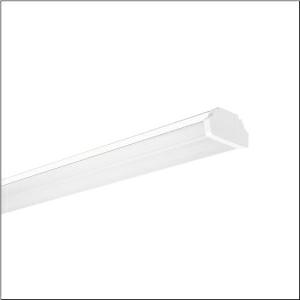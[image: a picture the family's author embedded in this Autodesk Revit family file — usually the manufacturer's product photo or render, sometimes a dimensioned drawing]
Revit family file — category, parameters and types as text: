
# Revit family: dus_31_gen_2_53bd812cv49xc2_ea29
name_source: partatom
category: Lighting Fixtures
units: mm (PartAtom-declared; Revit-internal decimal feet)

## family parameters
Cut with Voids When Loaded = No
Host = Face
Light Source = No
Part Type = Normal
Room Calculation Point = No
Round Connector Dimension = Use Diameter
Shared = No

## types (1)
- --- (1 x LED, 9240 lm, 49.9 W, 4000K)
    Apparent Load = 50 VA
    CIE Flux Codes = 47 80 95 93 100
    Color Rendering = 80
    Color Temperature = 4000K
    Default Elevation = 1800 mm
    Description = DUS 31 Gen.2, luminaire insert, of sheet steel, coil coated, white, length: 1.535mm, width: 81mm, height: 90mm, 5x system unit, system units: 307mm, LED rated luminous flux: 9.240lm, light colour: 840, SDCM (Standard Deviation of Colour Matching)MacAdam ≤ 3 SDCM (initial), control gear: ON/OFF Multilumen, CLOi, with plug, 3-pole, with phase selection, mains connection: 220..240V, AC, 50/60Hz, start of lifetime: 50W, end of service life: 61W, through-wiring accessed according to module size, primary optical cover: cover, of PMMA, light emission: direct distribution, primary light characteristic: symmetric, protection rating (complete): IP20, protection rating (LED compartment): IP50, insulation class (complete): insulation class I (protective earthing), certification: CE, ENEC, VDE, UKCA, impact resistance: IK03, permissible ambient temperature for indoor applications: -35..+40°C, corresponds to IFS (International Featured Standards) requirements for safety and quality in the food industry, reducing of maximum allowable ambient temperature of 5°C with ceiling mounting, packaging unit: 1 piece
    Height = 95 mm
    Lamp = 1 x LED
    Lamp Light Flux = 9240 lm
    Lamp Power = 49.9 W
    Lamp count = 1
    Length = 1535 mm
    Luminous efficacy = 185 lm/W
    Manufacturer = Siteco
    ModVariant = No
    Model = 53BD812CV49XC2
    Mounting Place = Ceiling
    Mounting Type = Pendant
    Number of Poles = 1
    OnlyDefault = Yes
    Power Factor = 1
    Product Name = DUS 31 Gen.2
    Product group = luminaire insert | ceiling pendant
    ProductGroupID = 901
    Protection Class = Protection class I
    Protection Degree = IP 20
    RLX_Detail_Level = 1
    RLX_Emergency_Light_Flux = 0 lm
    RLX_Emergency_Type = 0
    RLX_Emergency_Type_DB = No
    RlxData = <blob elided: 29869 chars, md5=17ca2b88>
    Socket = socket
    Standby Power = 0 W
    System Light Flux = 9240 lm
    System Power = 50 W
    Type Comments = factory setting: luminous flux: 100 % | (A | C | E) | 116 mA
    Type Image = l_1319596.jpg
    URL = http://relux.com
    VarID = @adj_051253
    Voltage = 0 V
    Weight = 0.00 kg
    Width = 81 mm

## geometry (parser evidence)
native form markers: Blend x4, Sweep x15
no freeform markers — native parametric forms only
